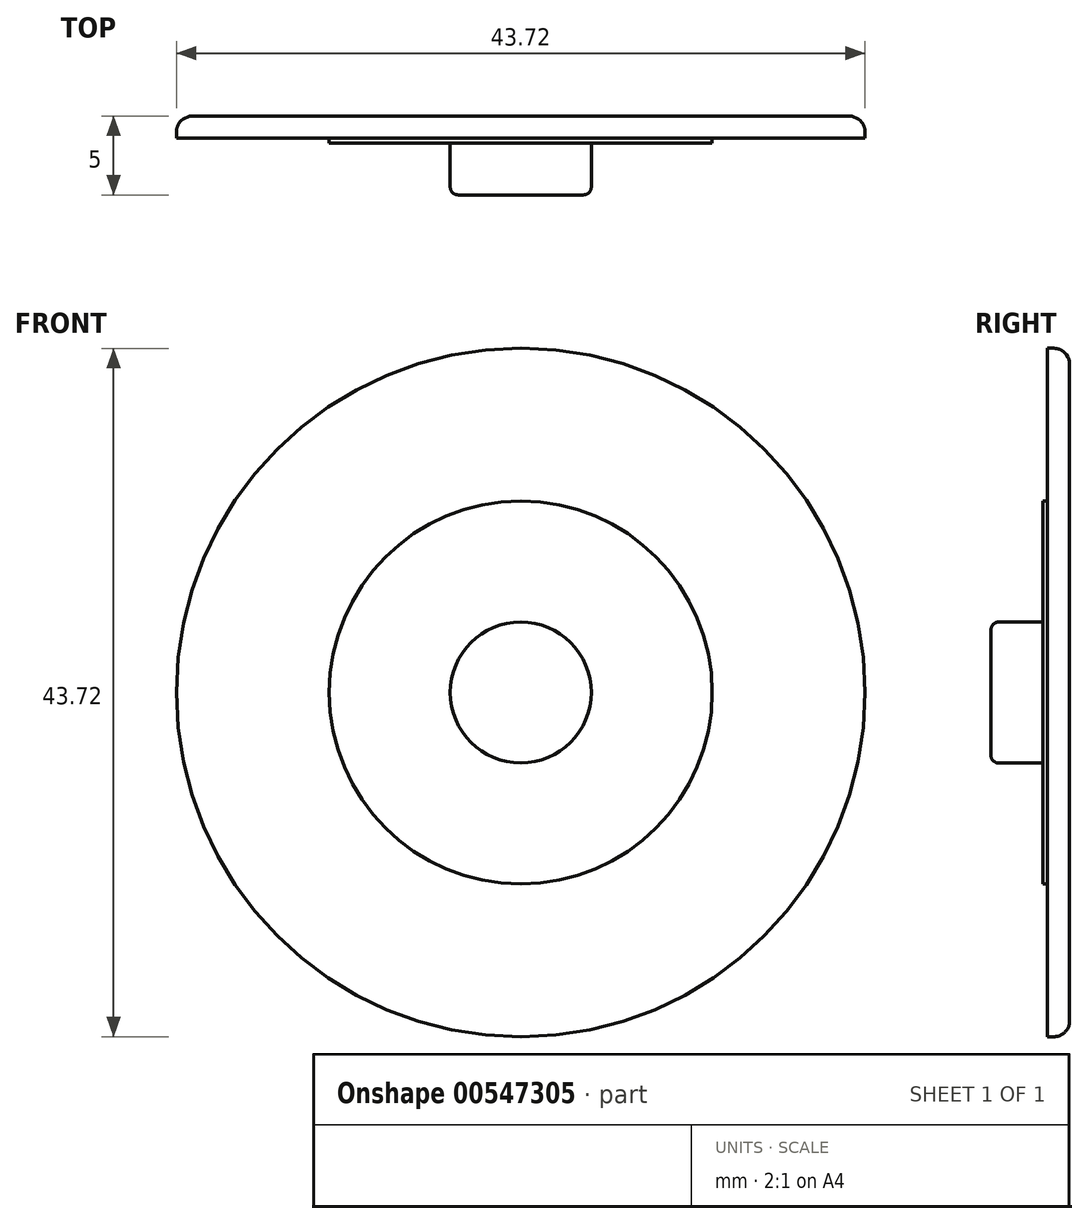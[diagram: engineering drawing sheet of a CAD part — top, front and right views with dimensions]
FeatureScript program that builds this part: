
annotation { "Feature Type Name" : "Feature", "Feature Type Description" : "" }
export const myFeature = defineFeature(function(context is Context, id is Id, definition is map)
    precondition{}
    {
        {
            var Q0;
            Q0=qCreatedBy(makeId("Front.planeOp"),FACE);
            var sketch = newSketch(context, id + "F0", { "sketchPlane" : qUnion([Q0])});
            skCircle(sketch, "E0", {"center": v(0, 0) * mm, "radius": 21.86 * mm});
            skSolve(sketch);
        }
        {
            var Q0;
            Q0=qCreatedBy(makeId("Front.planeOp"),FACE);
            var sketch = newSketch(context, id + "F1", { "sketchPlane" : qUnion([Q0])});
            skCircle(sketch, "E1", {"center": v(0, 0) * mm, "radius": 12.16 * mm});
            skSolve(sketch);
        }
        {
            var Q0;
            Q0=qCreatedBy(makeId("Front.planeOp"),FACE);
            var sketch = newSketch(context, id + "F2", { "sketchPlane" : qUnion([Q0])});
            skCircle(sketch, "E2", {"center": v(0, 0) * mm, "radius": 4.48 * mm});
            skSolve(sketch);
        }
        {
            var Q0;
            Q0 = qSketchRegion(id + "F2", true);
            extrude(context, id + "F3", {"entities" : qUnion([Q0]), "depth" : 5 * mm, "offsetDistance" : 25.4 * mm});
        }
        {
            var Q0;
            Q0 = qSketchRegion(id + "F1", true);
            extrude(context, id + "F4", {"entities" : qUnion([Q0]), "operationType" : NewBodyOperationType.ADD, "depth" : 1.7 * mm, "offsetDistance" : 25.4 * mm});
        }
        {
            var Q0;
            Q0 = qSketchRegion(id + "F0", true);
            extrude(context, id + "F5", {"entities" : qUnion([Q0]), "operationType" : NewBodyOperationType.ADD, "depth" : 1.4 * mm, "offsetDistance" : 25.4 * mm});
        }
        {
            var Q0;
            Q0=makeQuery(id+"F5.opExtrude","CAP_EDGE",EDGE,{"disambiguationData":[OSD([sQuery(id+"F0.wireOp",EDGE,"E0")])],"isStart":true});
            fillet(context, id + "F6", {"entities" : qUnion([Q0]), "radius" : 1 * mm, "tangentPropagation" : true, "allowEdgeOverflow" : false});
        }
        {
            var Q0;
            Q0=makeQuery(id+"F3.opExtrude","CAP_EDGE",EDGE,{"disambiguationData":[OSD([sQuery(id+"F2.wireOp",EDGE,"E2")])],"isStart":false});
            fillet(context, id + "F7", {"entities" : qUnion([Q0]), "radius" : 0.5 * mm, "tangentPropagation" : true, "allowEdgeOverflow" : false});
        }
    });
